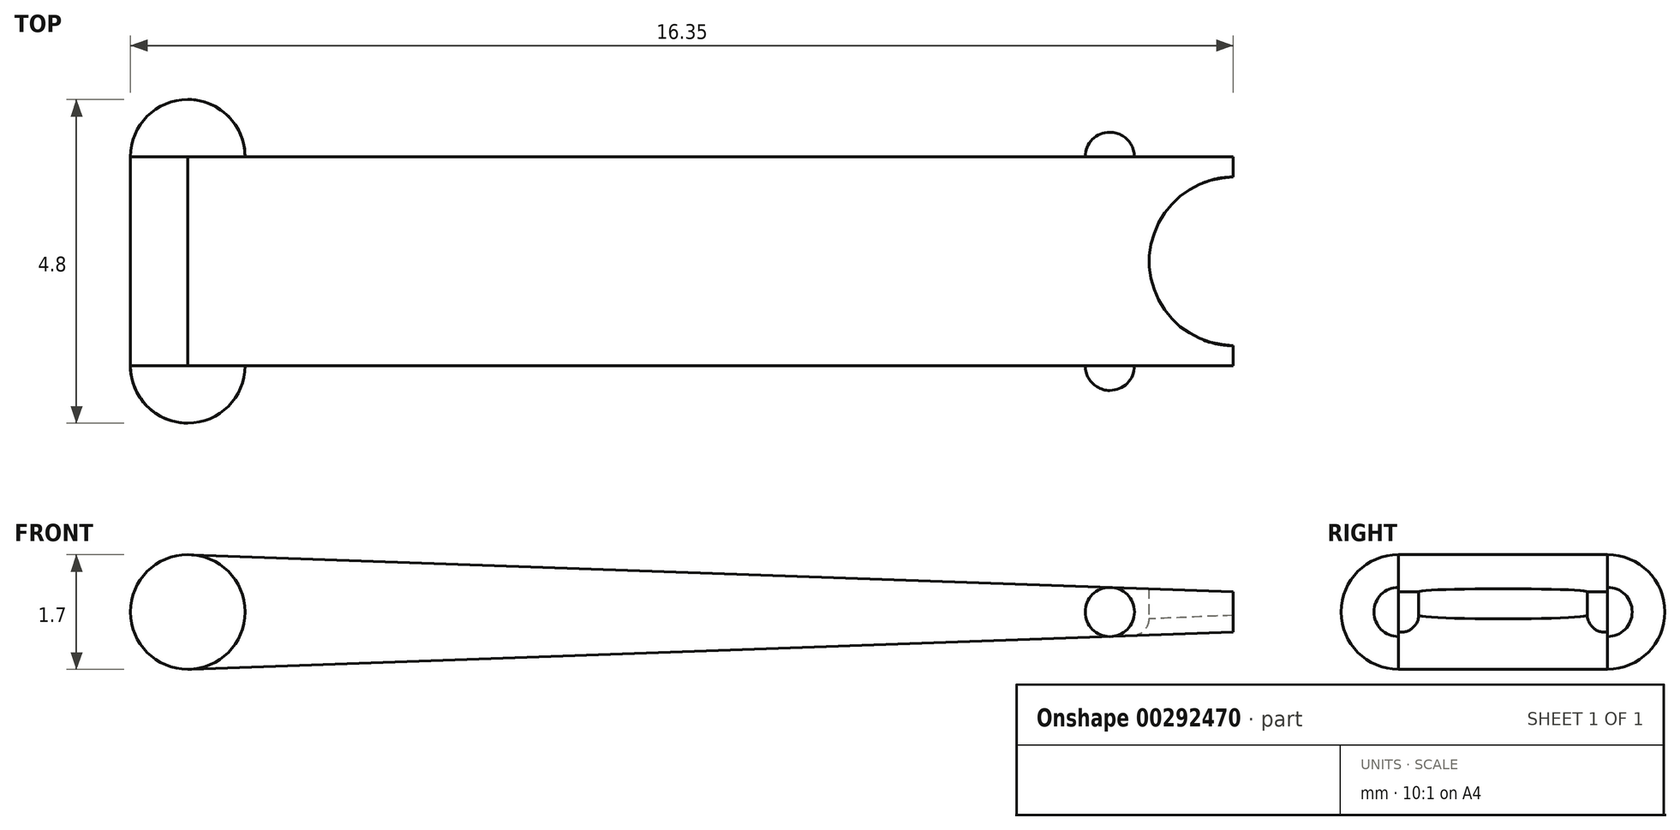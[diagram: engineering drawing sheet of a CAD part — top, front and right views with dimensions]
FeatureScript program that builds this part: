
annotation { "Feature Type Name" : "Feature", "Feature Type Description" : "" }
export const myFeature = defineFeature(function(context is Context, id is Id, definition is map)
    precondition{}
    {
        {
            var Q0;
            Q0=qCreatedBy(makeId("Top.planeOp"),FACE);
            var sketch = newSketch(context, id + "F0", { "sketchPlane" : qUnion([Q0])});
            skLineSegment(sketch, "E0", {"start": v(0, 0) * mm, "end": v(-13.67, 0) * mm});
            skLineSegment(sketch, "E1", {"start": v(0, -0.36) * mm, "end": v(0, 3.47) * mm});
            skLineSegment(sketch, "E2", {"start": v(0, 3.1) * mm, "end": v(-13.67, 3.1) * mm});
            skArc(sketch, "E3", {"start": v(-13.67, 3.95) * mm, "mid": v(-14.27, 3.7) * mm, "end": v(-14.52, 3.1) * mm});
            skArc(sketch, "E4", {"start": v(-14.52, 0) * mm, "mid": v(-14.27, -0.6) * mm, "end": v(-13.67, -0.85) * mm});
            skArc(sketch, "E5", {"start": v(-0.37, 0) * mm, "mid": v(-0.26, -0.26) * mm, "end": v(0, -0.36) * mm});
            skArc(sketch, "E6", {"start": v(0, 3.47) * mm, "mid": v(-0.26, 3.36) * mm, "end": v(-0.36, 3.1) * mm});
            skLineSegment(sketch, "E7", {"start": v(-14.52, 3.1) * mm, "end": v(-14.52, 0) * mm});
            skLineSegment(sketch, "E8", {"start": v(0, 3.1) * mm, "end": v(1.83, 3.1) * mm});
            skLineSegment(sketch, "E9", {"start": v(1.83, 3.1) * mm, "end": v(1.83, 0) * mm});
            skLineSegment(sketch, "E10", {"start": v(1.83, 0) * mm, "end": v(0, 0) * mm});
            skLineSegment(sketch, "E11", {"start": v(-13.67, 3.1) * mm, "end": v(-14.52, 3.1) * mm});
            skLineSegment(sketch, "E12", {"start": v(-13.67, 0) * mm, "end": v(-14.52, 0) * mm});
            skLineSegment(sketch, "E13", {"start": v(-13.67, 3.95) * mm, "end": v(-13.67, -0.85) * mm});
            skArc(sketch, "E14", {"start": v(1.83, 2.8) * mm, "mid": v(0.58, 1.55) * mm, "end": v(1.83, 0.3) * mm});
            skSolve(sketch);
        }
        {
            var Q0;
            {var subQ0=sQuery(id+"F0.wireOp",EDGE,"E3");Q0=makeQuery(id+"F0.imprint","IMPRINT",FACE,{"disambiguationData":[TD([[makeQuery(id+"F0.imprint","IMPRINT",EDGE,{"derivedFrom":subQ0}),1.0]])]});}
            var Q1;
            {var subQ0=sQuery(id+"F0.wireOp",EDGE,"E4");Q1=makeQuery(id+"F0.imprint","IMPRINT",FACE,{"disambiguationData":[TD([[makeQuery(id+"F0.imprint","IMPRINT",EDGE,{"derivedFrom":subQ0}),1.0]])]});}
            var Q2;
            Q2=sQuery(id+"F0.wireOp",EDGE,"E13");
            revolve(context, id + "F1", {"entities" : qUnion([Q0, Q1]), "axis" : qUnion([Q2]), "revolveType" : RevolveType.FULL});
        }
        {
            var Q0;
            {var subQ0=sQuery(id+"F0.wireOp",EDGE,"E6");Q0=makeQuery(id+"F0.imprint","IMPRINT",FACE,{"disambiguationData":[TD([[makeQuery(id+"F0.imprint","IMPRINT",EDGE,{"derivedFrom":subQ0}),1.0]])]});}
            var Q1;
            {var subQ3=sQuery(id+"F0.wireOp",EDGE,"E5");Q1=makeQuery(id+"F0.imprint","IMPRINT",FACE,{"disambiguationData":[TD([[makeQuery(id+"F0.imprint","IMPRINT",EDGE,{"derivedFrom":subQ3}),1.0]])]});}
            var Q2;
            Q2=sQuery(id+"F0.wireOp",EDGE,"E1");
            revolve(context, id + "F2", {"entities" : qUnion([Q0, Q1]), "axis" : qUnion([Q2]), "revolveType" : RevolveType.FULL});
        }
        {
            var Q0;
            Q0=makeQuery(id+"F1.opRevolve","SWEPT_FACE",FACE,{"disambiguationData":[OSD([sQuery(id+"F0.wireOp",EDGE,"E12")])]});
            var sketch = newSketch(context, id + "F3", { "sketchPlane" : qUnion([Q0])});
            skLineSegment(sketch, "E15", {"start": v(13.67, -0.85) * mm, "end": v(-1.83, -0.3) * mm});
            skLineSegment(sketch, "E16", {"start": v(-1.83, 0) * mm, "end": v(14.52, 0) * mm});
            skLineSegment(sketch, "E17", {"start": v(13.67, 0.85) * mm, "end": v(-1.83, 0.3) * mm});
            skLineSegment(sketch, "E18", {"start": v(-1.83, -0.3) * mm, "end": v(-1.83, 0.3) * mm});
            skArc(sketch, "E19", {"start": v(13.67, 0.85) * mm, "mid": v(14.52, -0.03) * mm, "end": v(13.61, -0.85) * mm});
            skSolve(sketch);
        }
        {
            var Q0;
            {var subQ0=sQuery(id+"F3.wireOp",EDGE,"E18");var subQ1=sQuery(id+"F3.wireOp",EDGE,"E16");var subQ2=makeQuery(id+"F3.imprint","INTERSECT",VERTEX,{"derivedFrom":[subQ1,subQ0]});Q0=makeQuery(id+"F3.imprint","IMPRINT",FACE,{"disambiguationData":[TD([[makeQuery(id+"F3.imprint","IMPRINT",EDGE,{"disambiguationData":[TD([[subQ2,-1.0]])],"derivedFrom":subQ0}),-1.0]])]});}
            var Q1;
            {var subQ0=sQuery(id+"F3.wireOp",EDGE,"E18");var subQ1=sQuery(id+"F3.wireOp",EDGE,"E15");var subQ2=makeQuery(id+"F3.imprint","INTERSECT",VERTEX,{"derivedFrom":[subQ1,subQ0]});Q1=makeQuery(id+"F3.imprint","IMPRINT",FACE,{"disambiguationData":[TD([[makeQuery(id+"F3.imprint","IMPRINT",EDGE,{"disambiguationData":[TD([[subQ2,-1.0]])],"derivedFrom":subQ0}),-1.0]])]});}
            var Q2;
            {var subQ0=sQuery(id+"F3.wireOp",EDGE,"kexO2Mrd-TqQ1-YHf7-cwiz-K5OhqgWDypU7");Q2=makeQuery(id+"F3.imprint","IMPRINT",FACE,{"disambiguationData":[TD([[makeQuery(id+"F3.imprint","IMPRINT",EDGE,{"derivedFrom":subQ0}),1.0]])]});}
            var Q3;
            {var subQ0=sQuery(id+"F3.wireOp",EDGE,"RqI69E63-UjgA-mUG7-lJKi-hYWhG313bSie");var subQ3=sQuery(id+"F3.wireOp",EDGE,"E16");var subQ4=makeQuery(id+"F3.imprint","INTERSECT",VERTEX,{"derivedFrom":[subQ0,subQ3]});Q3=makeQuery(id+"F3.imprint","IMPRINT",FACE,{"disambiguationData":[TD([[makeQuery(id+"F3.imprint","IMPRINT",EDGE,{"disambiguationData":[TD([[subQ4,1.0]])],"derivedFrom":subQ0}),1.0]])]});}
            var Q4;
            {var subQ0=sQuery(id+"F3.wireOp",EDGE,"E19");var subQ1=sQuery(id+"F3.wireOp",EDGE,"E16");var subQ2=makeQuery(id+"F3.imprint","INTERSECT",VERTEX,{"derivedFrom":[subQ1,subQ0]});Q4=makeQuery(id+"F3.imprint","IMPRINT",FACE,{"disambiguationData":[TD([[makeQuery(id+"F3.imprint","IMPRINT",EDGE,{"disambiguationData":[TD([[subQ2,1.0]])],"derivedFrom":subQ1}),1.0]])]});}
            var Q5;
            {var subQ0=sQuery(id+"F3.wireOp",EDGE,"E19");var subQ1=sQuery(id+"F3.wireOp",EDGE,"E15");var subQ2=makeQuery(id+"F3.imprint","INTERSECT",VERTEX,{"derivedFrom":[subQ1,subQ0]});Q5=makeQuery(id+"F3.imprint","IMPRINT",FACE,{"disambiguationData":[TD([[makeQuery(id+"F3.imprint","IMPRINT",EDGE,{"disambiguationData":[TD([[subQ2,-1.0]])],"derivedFrom":subQ0}),1.0]])]});}
            var Q6;
            Q6=makeQuery(id+"F1.opRevolve","SWEPT_FACE",FACE,{"disambiguationData":[OSD([sQuery(id+"F0.wireOp",EDGE,"E11")])]});
            extrude(context, id + "F4", {"entities" : qUnion([Q0, Q1, Q2, Q3, Q4, Q5]), "endBound" : BoundingType.UP_TO_SURFACE, "endBoundEntityFace" : qUnion([Q6]), "depth" : 25 * mm});
        }
        {
            var Q0;
            {var subQ0=sQuery(id+"F0.wireOp",EDGE,"E14");Q0=makeQuery(id+"F0.imprint","IMPRINT",FACE,{"disambiguationData":[TD([[makeQuery(id+"F0.imprint","IMPRINT",EDGE,{"derivedFrom":subQ0}),1.0]])]});}
            extrude(context, id + "F5", {"entities" : qUnion([Q0]), "operationType" : NewBodyOperationType.REMOVE, "endBound" : BoundingType.SYMMETRIC, "depth" : 1 * mm});
        }
        {
            var Q0;
            Q0=makeQuery(id+"F5.boolean.opBoolean","INTERSECT",EDGE,{"derivedFrom":[makeQuery(id+"F4.opExtrude","SWEPT_FACE",FACE,{"disambiguationData":[OSD([sQuery(id+"F3.wireOp",EDGE,"E15")])]}),makeQuery(id+"F5.opExtrude","SWEPT_FACE",FACE,{"disambiguationData":[OSD([sQuery(id+"F0.wireOp",EDGE,"E14")])]})]});
            fillet(context, id + "F6", {"entities" : qUnion([Q0]), "radius" : 0.25 * mm, "tangentPropagation" : true, "allowEdgeOverflow" : false});
        }
    });
